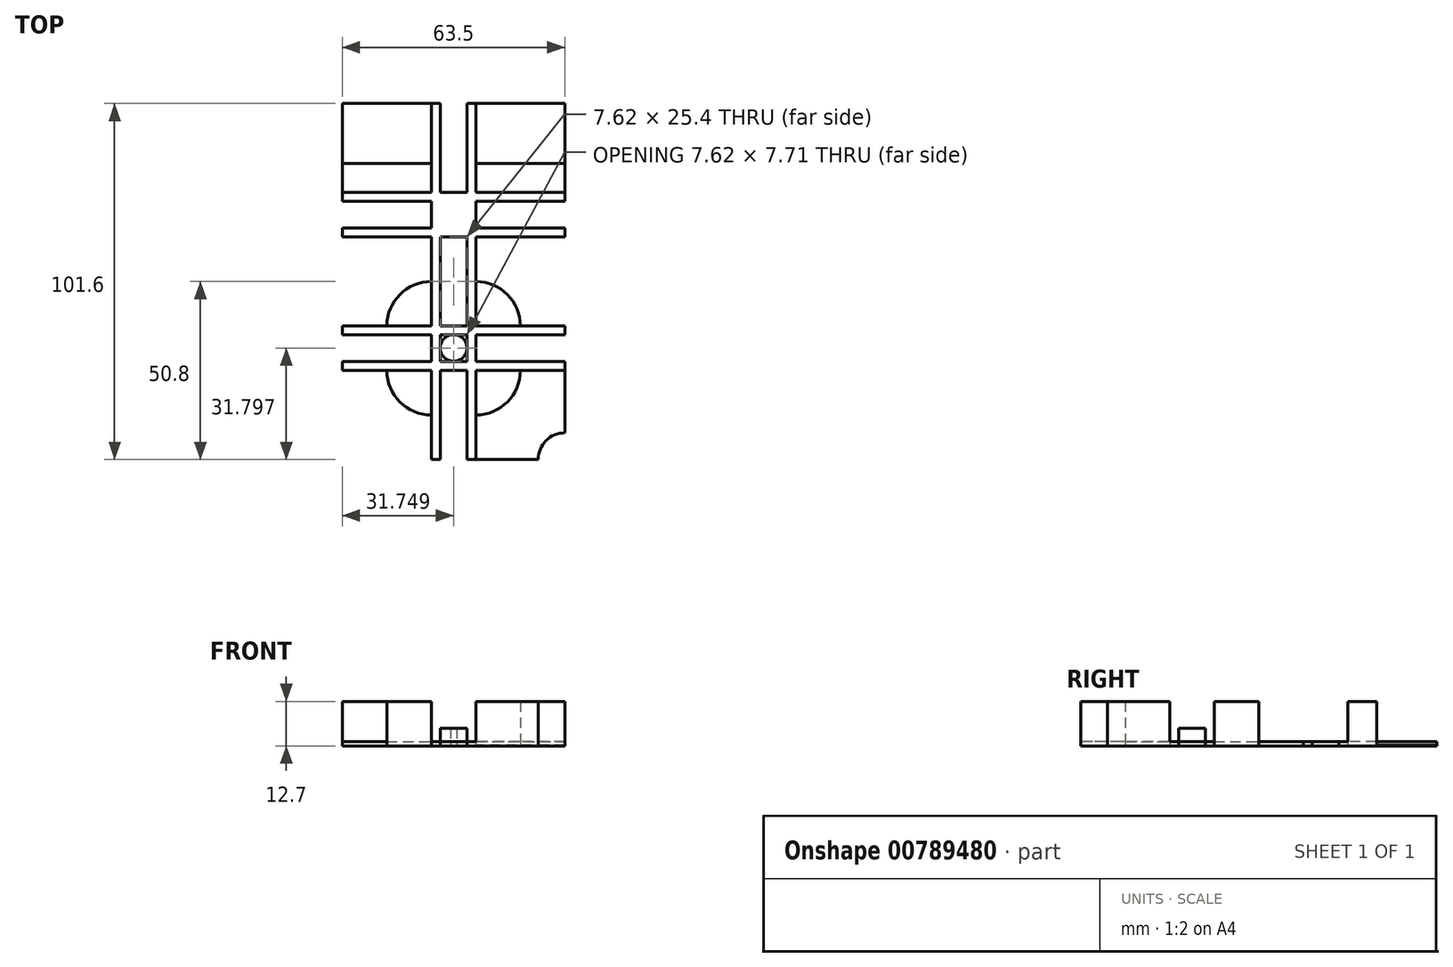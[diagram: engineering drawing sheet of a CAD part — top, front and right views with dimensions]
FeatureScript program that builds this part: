
annotation { "Feature Type Name" : "Feature", "Feature Type Description" : "" }
export const myFeature = defineFeature(function(context is Context, id is Id, definition is map)
    precondition{}
    {
        {
            var Q0;
            Q0=qCreatedBy(makeId("Top.planeOp"),FACE);
            var sketch = newSketch(context, id + "F0", { "sketchPlane" : qUnion([Q0])});
            skLineSegment(sketch, "E0.bottom", {"start": v(6.32, 50.8) * mm, "end": v(-19.08, 50.8) * mm});
            skLineSegment(sketch, "E0.top", {"start": v(6.32, 25.4) * mm, "end": v(-19.08, 25.4) * mm});
            skLineSegment(sketch, "E0.left", {"start": v(6.32, 50.8) * mm, "end": v(6.32, 25.4) * mm});
            skLineSegment(sketch, "E0.right", {"start": v(-19.08, 50.8) * mm, "end": v(-19.08, 25.4) * mm});
            skPoint(sketch, "E0.middle", {"position": v(-6.38, 38.1) * mm});
            skLineSegment(sketch, "E1.bottom", {"start": v(44.42, 25.4) * mm, "end": v(19.02, 25.4) * mm});
            skLineSegment(sketch, "E1.top", {"start": v(44.42, 50.8) * mm, "end": v(19.02, 50.8) * mm});
            skLineSegment(sketch, "E1.left", {"start": v(44.42, 25.4) * mm, "end": v(44.42, 50.8) * mm});
            skLineSegment(sketch, "E1.right", {"start": v(19.02, 25.4) * mm, "end": v(19.02, 50.8) * mm});
            skPoint(sketch, "E1.middle", {"position": v(31.72, 38.1) * mm});
            skLineSegment(sketch, "E2.bottom", {"start": v(-19.08, -12.7) * mm, "end": v(6.32, -12.7) * mm});
            skLineSegment(sketch, "E2.top", {"start": v(-19.08, 12.7) * mm, "end": v(6.32, 12.7) * mm});
            skLineSegment(sketch, "E2.left", {"start": v(-19.08, -12.7) * mm, "end": v(-19.08, 12.7) * mm});
            skLineSegment(sketch, "E2.right", {"start": v(6.32, -12.7) * mm, "end": v(6.32, 12.7) * mm});
            skPoint(sketch, "E2.middle", {"position": v(-6.38, 0) * mm});
            skLineSegment(sketch, "E3.bottom", {"start": v(44.42, -12.7) * mm, "end": v(19.02, -12.7) * mm});
            skLineSegment(sketch, "E3.top", {"start": v(44.42, 12.7) * mm, "end": v(19.02, 12.7) * mm});
            skLineSegment(sketch, "E3.left", {"start": v(44.42, -12.7) * mm, "end": v(44.42, 12.7) * mm});
            skLineSegment(sketch, "E3.right", {"start": v(19.02, -12.7) * mm, "end": v(19.02, 12.7) * mm});
            skPoint(sketch, "E3.middle", {"position": v(31.72, 0) * mm});
            skLineSegment(sketch, "E4.bottom", {"start": v(44.42, -50.8) * mm, "end": v(19.02, -50.8) * mm});
            skLineSegment(sketch, "E4.top", {"start": v(44.42, -25.4) * mm, "end": v(19.02, -25.4) * mm});
            skLineSegment(sketch, "E4.left", {"start": v(44.42, -50.8) * mm, "end": v(44.42, -25.4) * mm});
            skLineSegment(sketch, "E4.right", {"start": v(19.02, -50.8) * mm, "end": v(19.02, -25.4) * mm});
            skPoint(sketch, "E4.middle", {"position": v(31.72, -38.1) * mm});
            skPoint(sketch, "E4.middle.positionSnap0", {"position": v(31.72, -12.7) * mm});
            skPoint(sketch, "E4.centerSnap0", {"position": v(31.72, -12.7) * mm});
            skLineSegment(sketch, "E5.bottom", {"start": v(-19.08, -25.4) * mm, "end": v(6.32, -25.4) * mm});
            skLineSegment(sketch, "E5.top", {"start": v(-19.08, -50.8) * mm, "end": v(6.32, -50.8) * mm});
            skLineSegment(sketch, "E5.left", {"start": v(-19.08, -25.4) * mm, "end": v(-19.08, -50.8) * mm});
            skLineSegment(sketch, "E5.right", {"start": v(6.32, -25.4) * mm, "end": v(6.32, -50.8) * mm});
            skPoint(sketch, "E5.middle", {"position": v(-6.38, -38.1) * mm});
            skPoint(sketch, "E5.middle.positionSnap0", {"position": v(-6.38, -12.7) * mm});
            skPoint(sketch, "E5.middle.positionSnap1", {"position": v(19.02, -38.1) * mm});
            skPoint(sketch, "E5.centerSnap0", {"position": v(-6.38, -12.7) * mm});
            skPoint(sketch, "E5.centerSnap1", {"position": v(19.02, -38.1) * mm});
            skLineSegment(sketch, "E6.bottom", {"start": v(6.32, 50.8) * mm, "end": v(8.86, 50.8) * mm});
            skLineSegment(sketch, "E6.top", {"start": v(6.32, -50.8) * mm, "end": v(8.86, -50.8) * mm});
            skLineSegment(sketch, "E6.left", {"start": v(6.32, 50.8) * mm, "end": v(6.32, -50.8) * mm});
            skLineSegment(sketch, "E6.right", {"start": v(8.86, 50.8) * mm, "end": v(8.86, -50.8) * mm});
            skLineSegment(sketch, "E7.bottom", {"start": v(19.02, 50.8) * mm, "end": v(16.48, 50.8) * mm});
            skLineSegment(sketch, "E7.top", {"start": v(19.02, -50.8) * mm, "end": v(16.48, -50.8) * mm});
            skLineSegment(sketch, "E7.left", {"start": v(19.02, 50.8) * mm, "end": v(19.02, -50.8) * mm});
            skLineSegment(sketch, "E7.right", {"start": v(16.48, 50.8) * mm, "end": v(16.48, -50.8) * mm});
            skLineSegment(sketch, "E8.bottom", {"start": v(-19.08, 25.4) * mm, "end": v(44.42, 25.4) * mm});
            skLineSegment(sketch, "E8.top", {"start": v(-19.08, 22.86) * mm, "end": v(44.42, 22.86) * mm});
            skLineSegment(sketch, "E8.left", {"start": v(-19.08, 25.4) * mm, "end": v(-19.08, 22.86) * mm});
            skLineSegment(sketch, "E8.right", {"start": v(44.42, 25.4) * mm, "end": v(44.42, 22.86) * mm});
            skLineSegment(sketch, "E9.bottom", {"start": v(-19.08, 12.7) * mm, "end": v(44.42, 12.7) * mm});
            skLineSegment(sketch, "E9.top", {"start": v(-19.08, 15.24) * mm, "end": v(44.42, 15.24) * mm});
            skLineSegment(sketch, "E9.left", {"start": v(-19.08, 12.7) * mm, "end": v(-19.08, 15.24) * mm});
            skLineSegment(sketch, "E9.right", {"start": v(44.42, 12.7) * mm, "end": v(44.42, 15.24) * mm});
            skLineSegment(sketch, "E10.bottom", {"start": v(-19.08, -25.4) * mm, "end": v(44.42, -25.4) * mm});
            skLineSegment(sketch, "E10.top", {"start": v(-19.08, -22.86) * mm, "end": v(44.42, -22.86) * mm});
            skLineSegment(sketch, "E10.left", {"start": v(-19.08, -25.4) * mm, "end": v(-19.08, -22.86) * mm});
            skLineSegment(sketch, "E10.right", {"start": v(44.42, -25.4) * mm, "end": v(44.42, -22.86) * mm});
            skLineSegment(sketch, "E11.bottom", {"start": v(-19.08, -12.7) * mm, "end": v(44.42, -12.7) * mm});
            skLineSegment(sketch, "E11.top", {"start": v(-19.08, -15.24) * mm, "end": v(44.42, -15.24) * mm});
            skLineSegment(sketch, "E11.left", {"start": v(-19.08, -12.7) * mm, "end": v(-19.08, -15.24) * mm});
            skLineSegment(sketch, "E11.right", {"start": v(44.42, -12.7) * mm, "end": v(44.42, -15.24) * mm});
            skCircle(sketch, "E12", {"center": v(12.67, -18.95) * mm, "radius": 3.81 * mm});
            skPoint(sketch, "E12.centerSnap0", {"position": v(12.67, -15.24) * mm});
            skLineSegment(sketch, "E13", {"start": v(-19.08, 33.65) * mm, "end": v(6.32, 33.65) * mm});
            skLineSegment(sketch, "E14", {"start": v(19.02, 33.65) * mm, "end": v(44.42, 33.65) * mm});
            skArc(sketch, "E15", {"start": v(-2.7, -3.75) * mm, "mid": v(1.44, -0.98) * mm, "end": v(6.32, 0) * mm});
            skArc(sketch, "E16", {"start": v(-2.7, -3.75) * mm, "mid": v(-5.42, -7.86) * mm, "end": v(-6.38, -12.7) * mm});
            skArc(sketch, "E17", {"start": v(28.34, -4.08) * mm, "mid": v(30.85, -8.07) * mm, "end": v(31.72, -12.7) * mm});
            skArc(sketch, "E18", {"start": v(28.34, -4.08) * mm, "mid": v(24.1, -1.06) * mm, "end": v(19.02, 0) * mm});
            skArc(sketch, "E19", {"start": v(-1.73, -35.23) * mm, "mid": v(-5.16, -30.84) * mm, "end": v(-6.38, -25.4) * mm});
            skArc(sketch, "E20", {"start": v(-1.73, -35.23) * mm, "mid": v(2.05, -37.36) * mm, "end": v(6.32, -38.1) * mm});
            skArc(sketch, "E21", {"start": v(28.65, -33.67) * mm, "mid": v(30.93, -29.81) * mm, "end": v(31.72, -25.4) * mm});
            skArc(sketch, "E22", {"start": v(28.65, -33.67) * mm, "mid": v(24.32, -36.94) * mm, "end": v(19.02, -38.1) * mm});
            skArc(sketch, "E23", {"start": v(39.2, -45.25) * mm, "mid": v(41.6, -43.72) * mm, "end": v(44.42, -43.18) * mm});
            skArc(sketch, "E24", {"start": v(39.2, -45.25) * mm, "mid": v(37.42, -47.78) * mm, "end": v(36.8, -50.8) * mm});
            skArc(sketch, "E25", {"start": v(-13.68, -45.43) * mm, "mid": v(-12.04, -47.9) * mm, "end": v(-11.46, -50.8) * mm});
            skArc(sketch, "E26", {"start": v(-13.68, -45.43) * mm, "mid": v(-16.16, -43.76) * mm, "end": v(-19.08, -43.18) * mm});
            skArc(sketch, "E27", {"start": v(38.84, 7.5) * mm, "mid": v(37.33, 9.9) * mm, "end": v(36.8, 12.7) * mm});
            skArc(sketch, "E28", {"start": v(38.84, 7.5) * mm, "mid": v(41.38, 5.71) * mm, "end": v(44.42, 5.08) * mm});
            skArc(sketch, "E29", {"start": v(-13.86, 7.15) * mm, "mid": v(-12.09, 9.68) * mm, "end": v(-11.46, 12.7) * mm});
            skArc(sketch, "E30", {"start": v(-13.86, 7.15) * mm, "mid": v(-16.27, 5.62) * mm, "end": v(-19.08, 5.08) * mm});
            skSolve(sketch);
        }
        {
            var Q0;
            {var subQ0=sQuery(id+"F0.wireOp",EDGE,"E12");var subQ1=sQuery(id+"F0.wireOp",EDGE,"E11.top");var subQ2=makeQuery(id+"F0.imprint","INTERSECT",VERTEX,{"disambiguationData":[OD(0.0)],"derivedFrom":[subQ1,subQ0]});Q0=makeQuery(id+"F0.imprint","IMPRINT",FACE,{"disambiguationData":[TD([[makeQuery(id+"F0.imprint","IMPRINT",EDGE,{"disambiguationData":[TD([[subQ2,1.0]])],"derivedFrom":subQ1}),-1.0]])]});}
            extrude(context, id + "F1", {"entities" : qUnion([Q0]), "depth" : 5.08 * mm, "offsetDistance" : 25.4 * mm});
        }
        {
            var Q0;
            {var subQ0=sQuery(id+"F0.wireOp",EDGE,"E6.bottom");Q0=makeQuery(id+"F0.imprint","IMPRINT",FACE,{"disambiguationData":[TD([[makeQuery(id+"F0.imprint","IMPRINT",EDGE,{"derivedFrom":subQ0}),-1.0]])]});}
            var Q1;
            {var subQ0=sQuery(id+"F0.wireOp",EDGE,"E7.bottom");Q1=makeQuery(id+"F0.imprint","IMPRINT",FACE,{"disambiguationData":[TD([[makeQuery(id+"F0.imprint","IMPRINT",EDGE,{"derivedFrom":subQ0}),1.0]])]});}
            var Q2;
            {var subQ0=sQuery(id+"F0.wireOp",EDGE,"E8.top");var subQ1=sQuery(id+"F0.wireOp",EDGE,"E6.right");var subQ2=makeQuery(id+"F0.imprint","INTERSECT",VERTEX,{"derivedFrom":[subQ1,subQ0]});Q2=makeQuery(id+"F0.imprint","IMPRINT",FACE,{"disambiguationData":[TD([[makeQuery(id+"F0.imprint","IMPRINT",EDGE,{"disambiguationData":[TD([[subQ2,-1.0]])],"derivedFrom":subQ1}),1.0]])]});}
            var Q3;
            {var subQ0=sQuery(id+"F0.wireOp",EDGE,"E8.bottom");var subQ1=sQuery(id+"F0.wireOp",EDGE,"E6.right");var subQ2=makeQuery(id+"F0.imprint","INTERSECT",VERTEX,{"derivedFrom":[subQ1,subQ0]});Q3=makeQuery(id+"F0.imprint","IMPRINT",FACE,{"disambiguationData":[TD([[makeQuery(id+"F0.imprint","IMPRINT",EDGE,{"disambiguationData":[TD([[subQ2,-1.0]])],"derivedFrom":subQ1}),1.0]])]});}
            var Q4;
            {var subQ0=sQuery(id+"F0.wireOp",EDGE,"E8.bottom");var subQ5=sQuery(id+"F0.wireOp",EDGE,"E6.right");var subQ6=makeQuery(id+"F0.imprint","INTERSECT",VERTEX,{"derivedFrom":[subQ5,subQ0]});Q4=makeQuery(id+"F0.imprint","IMPRINT",FACE,{"disambiguationData":[TD([[makeQuery(id+"F0.imprint","IMPRINT",EDGE,{"disambiguationData":[TD([[subQ6,-1.0]])],"derivedFrom":subQ5}),-1.0]])]});}
            var Q5;
            {var subQ0=sQuery(id+"F0.wireOp",EDGE,"E0.top");Q5=makeQuery(id+"F0.imprint","IMPRINT",FACE,{"disambiguationData":[TD([[makeQuery(id+"F0.imprint","IMPRINT",EDGE,{"derivedFrom":subQ0}),1.0]])]});}
            var Q6;
            {var subQ0=sQuery(id+"F0.wireOp",EDGE,"E9.top");var subQ1=sQuery(id+"F0.wireOp",EDGE,"E6.left");var subQ2=makeQuery(id+"F0.imprint","INTERSECT",VERTEX,{"derivedFrom":[subQ1,subQ0]});Q6=makeQuery(id+"F0.imprint","IMPRINT",FACE,{"disambiguationData":[TD([[makeQuery(id+"F0.imprint","IMPRINT",EDGE,{"disambiguationData":[TD([[subQ2,1.0]])],"derivedFrom":subQ1}),1.0]])]});}
            var Q7;
            {var subQ0=sQuery(id+"F0.wireOp",EDGE,"E8.top");var subQ1=sQuery(id+"F0.wireOp",EDGE,"E7.left");var subQ2=makeQuery(id+"F0.imprint","INTERSECT",VERTEX,{"derivedFrom":[subQ1,subQ0]});Q7=makeQuery(id+"F0.imprint","IMPRINT",FACE,{"disambiguationData":[TD([[makeQuery(id+"F0.imprint","IMPRINT",EDGE,{"disambiguationData":[TD([[subQ2,-1.0]])],"derivedFrom":subQ1}),-1.0]])]});}
            var Q8;
            {var subQ0=sQuery(id+"F0.wireOp",EDGE,"E1.bottom");Q8=makeQuery(id+"F0.imprint","IMPRINT",FACE,{"disambiguationData":[TD([[makeQuery(id+"F0.imprint","IMPRINT",EDGE,{"derivedFrom":subQ0}),1.0]])]});}
            var Q9;
            {var subQ0=sQuery(id+"F0.wireOp",EDGE,"E8.bottom");var subQ5=sQuery(id+"F0.wireOp",EDGE,"E7.right");var subQ6=makeQuery(id+"F0.imprint","INTERSECT",VERTEX,{"derivedFrom":[subQ5,subQ0]});Q9=makeQuery(id+"F0.imprint","IMPRINT",FACE,{"disambiguationData":[TD([[makeQuery(id+"F0.imprint","IMPRINT",EDGE,{"disambiguationData":[TD([[subQ6,-1.0]])],"derivedFrom":subQ5}),1.0]])]});}
            var Q10;
            {var subQ0=sQuery(id+"F0.wireOp",EDGE,"E9.right");Q10=makeQuery(id+"F0.imprint","IMPRINT",FACE,{"disambiguationData":[TD([[makeQuery(id+"F0.imprint","IMPRINT",EDGE,{"derivedFrom":subQ0}),1.0]])]});}
            var Q11;
            {var subQ0=sQuery(id+"F0.wireOp",EDGE,"E9.bottom");var subQ5=sQuery(id+"F0.wireOp",EDGE,"E7.right");var subQ6=makeQuery(id+"F0.imprint","INTERSECT",VERTEX,{"derivedFrom":[subQ5,subQ0]});Q11=makeQuery(id+"F0.imprint","IMPRINT",FACE,{"disambiguationData":[TD([[makeQuery(id+"F0.imprint","IMPRINT",EDGE,{"disambiguationData":[TD([[subQ6,1.0]])],"derivedFrom":subQ5}),1.0]])]});}
            var Q12;
            {var subQ3=sQuery(id+"F0.wireOp",EDGE,"E9.bottom");var subQ5=sQuery(id+"F0.wireOp",EDGE,"E6.right");var subQ6=makeQuery(id+"F0.imprint","INTERSECT",VERTEX,{"derivedFrom":[subQ5,subQ3]});Q12=makeQuery(id+"F0.imprint","IMPRINT",FACE,{"disambiguationData":[TD([[makeQuery(id+"F0.imprint","IMPRINT",EDGE,{"disambiguationData":[TD([[subQ6,1.0]])],"derivedFrom":subQ5}),-1.0]])]});}
            var Q13;
            {var subQ0=sQuery(id+"F0.wireOp",EDGE,"E9.left");Q13=makeQuery(id+"F0.imprint","IMPRINT",FACE,{"disambiguationData":[TD([[makeQuery(id+"F0.imprint","IMPRINT",EDGE,{"derivedFrom":subQ0}),-1.0]])]});}
            var Q14;
            {var subQ0=sQuery(id+"F0.wireOp",EDGE,"E9.bottom");var subQ1=sQuery(id+"F0.wireOp",EDGE,"E6.right");var subQ2=makeQuery(id+"F0.imprint","INTERSECT",VERTEX,{"derivedFrom":[subQ1,subQ0]});Q14=makeQuery(id+"F0.imprint","IMPRINT",FACE,{"disambiguationData":[TD([[makeQuery(id+"F0.imprint","IMPRINT",EDGE,{"disambiguationData":[TD([[subQ2,1.0]])],"derivedFrom":subQ1}),1.0]])]});}
            var Q15;
            {var subQ0=sQuery(id+"F0.wireOp",EDGE,"E9.bottom");var subQ1=sQuery(id+"F0.wireOp",EDGE,"E6.right");var subQ2=makeQuery(id+"F0.imprint","INTERSECT",VERTEX,{"derivedFrom":[subQ1,subQ0]});Q15=makeQuery(id+"F0.imprint","IMPRINT",FACE,{"disambiguationData":[TD([[makeQuery(id+"F0.imprint","IMPRINT",EDGE,{"disambiguationData":[TD([[subQ2,-1.0]])],"derivedFrom":subQ1}),-1.0]])]});}
            var Q16;
            {var subQ0=sQuery(id+"F0.wireOp",EDGE,"E9.bottom");var subQ1=sQuery(id+"F0.wireOp",EDGE,"E7.right");var subQ2=makeQuery(id+"F0.imprint","INTERSECT",VERTEX,{"derivedFrom":[subQ1,subQ0]});Q16=makeQuery(id+"F0.imprint","IMPRINT",FACE,{"disambiguationData":[TD([[makeQuery(id+"F0.imprint","IMPRINT",EDGE,{"disambiguationData":[TD([[subQ2,-1.0]])],"derivedFrom":subQ1}),1.0]])]});}
            var Q17;
            {var subQ3=sQuery(id+"F0.wireOp",EDGE,"E11.left");Q17=makeQuery(id+"F0.imprint","IMPRINT",FACE,{"disambiguationData":[TD([[makeQuery(id+"F0.imprint","IMPRINT",EDGE,{"derivedFrom":subQ3}),1.0]])]});}
            var Q18;
            {var subQ0=sQuery(id+"F0.wireOp",EDGE,"E11.bottom");var subQ5=sQuery(id+"F0.wireOp",EDGE,"E6.right");var subQ6=makeQuery(id+"F0.imprint","INTERSECT",VERTEX,{"derivedFrom":[subQ5,subQ0]});Q18=makeQuery(id+"F0.imprint","IMPRINT",FACE,{"disambiguationData":[TD([[makeQuery(id+"F0.imprint","IMPRINT",EDGE,{"disambiguationData":[TD([[subQ6,-1.0]])],"derivedFrom":subQ5}),-1.0]])]});}
            var Q19;
            {var subQ0=sQuery(id+"F0.wireOp",EDGE,"E11.bottom");var subQ7=sQuery(id+"F0.wireOp",EDGE,"E6.right");var subQ8=makeQuery(id+"F0.imprint","INTERSECT",VERTEX,{"derivedFrom":[subQ7,subQ0]});Q19=makeQuery(id+"F0.imprint","IMPRINT",FACE,{"disambiguationData":[TD([[makeQuery(id+"F0.imprint","IMPRINT",EDGE,{"disambiguationData":[TD([[subQ8,-1.0]])],"derivedFrom":subQ7}),1.0]])]});}
            var Q20;
            {var subQ0=sQuery(id+"F0.wireOp",EDGE,"E11.bottom");var subQ5=sQuery(id+"F0.wireOp",EDGE,"E7.right");var subQ6=makeQuery(id+"F0.imprint","INTERSECT",VERTEX,{"derivedFrom":[subQ5,subQ0]});Q20=makeQuery(id+"F0.imprint","IMPRINT",FACE,{"disambiguationData":[TD([[makeQuery(id+"F0.imprint","IMPRINT",EDGE,{"disambiguationData":[TD([[subQ6,-1.0]])],"derivedFrom":subQ5}),1.0]])]});}
            var Q21;
            {var subQ3=sQuery(id+"F0.wireOp",EDGE,"E11.right");Q21=makeQuery(id+"F0.imprint","IMPRINT",FACE,{"disambiguationData":[TD([[makeQuery(id+"F0.imprint","IMPRINT",EDGE,{"derivedFrom":subQ3}),-1.0]])]});}
            var Q22;
            {var subQ1=sQuery(id+"F0.wireOp",EDGE,"E7.left");var subQ6=sQuery(id+"F0.wireOp",EDGE,"E11.top");var subQ7=makeQuery(id+"F0.imprint","INTERSECT",VERTEX,{"derivedFrom":[subQ1,subQ6]});Q22=makeQuery(id+"F0.imprint","IMPRINT",FACE,{"disambiguationData":[TD([[makeQuery(id+"F0.imprint","IMPRINT",EDGE,{"disambiguationData":[TD([[subQ7,-1.0]])],"derivedFrom":subQ1}),-1.0]])]});}
            var Q23;
            {var subQ2=sQuery(id+"F0.wireOp",EDGE,"E11.top");var subQ4=sQuery(id+"F0.wireOp",EDGE,"E6.left");var subQ5=makeQuery(id+"F0.imprint","INTERSECT",VERTEX,{"derivedFrom":[subQ4,subQ2]});Q23=makeQuery(id+"F0.imprint","IMPRINT",FACE,{"disambiguationData":[TD([[makeQuery(id+"F0.imprint","IMPRINT",EDGE,{"disambiguationData":[TD([[subQ5,-1.0]])],"derivedFrom":subQ4}),1.0]])]});}
            var Q24;
            {var subQ0=sQuery(id+"F0.wireOp",EDGE,"E10.bottom");var subQ1=sQuery(id+"F0.wireOp",EDGE,"E6.right");var subQ2=makeQuery(id+"F0.imprint","INTERSECT",VERTEX,{"derivedFrom":[subQ1,subQ0]});Q24=makeQuery(id+"F0.imprint","IMPRINT",FACE,{"disambiguationData":[TD([[makeQuery(id+"F0.imprint","IMPRINT",EDGE,{"disambiguationData":[TD([[subQ2,1.0]])],"derivedFrom":subQ1}),1.0]])]});}
            var Q25;
            {var subQ0=sQuery(id+"F0.wireOp",EDGE,"E10.bottom");var subQ5=sQuery(id+"F0.wireOp",EDGE,"E6.right");var subQ6=makeQuery(id+"F0.imprint","INTERSECT",VERTEX,{"derivedFrom":[subQ5,subQ0]});Q25=makeQuery(id+"F0.imprint","IMPRINT",FACE,{"disambiguationData":[TD([[makeQuery(id+"F0.imprint","IMPRINT",EDGE,{"disambiguationData":[TD([[subQ6,1.0]])],"derivedFrom":subQ5}),-1.0]])]});}
            var Q26;
            {var subQ0=sQuery(id+"F0.wireOp",EDGE,"E10.left");Q26=makeQuery(id+"F0.imprint","IMPRINT",FACE,{"disambiguationData":[TD([[makeQuery(id+"F0.imprint","IMPRINT",EDGE,{"derivedFrom":subQ0}),-1.0]])]});}
            var Q27;
            {var subQ3=sQuery(id+"F0.wireOp",EDGE,"E10.right");Q27=makeQuery(id+"F0.imprint","IMPRINT",FACE,{"disambiguationData":[TD([[makeQuery(id+"F0.imprint","IMPRINT",EDGE,{"derivedFrom":subQ3}),1.0]])]});}
            var Q28;
            {var subQ0=sQuery(id+"F0.wireOp",EDGE,"E10.bottom");var subQ5=sQuery(id+"F0.wireOp",EDGE,"E7.right");var subQ6=makeQuery(id+"F0.imprint","INTERSECT",VERTEX,{"derivedFrom":[subQ5,subQ0]});Q28=makeQuery(id+"F0.imprint","IMPRINT",FACE,{"disambiguationData":[TD([[makeQuery(id+"F0.imprint","IMPRINT",EDGE,{"disambiguationData":[TD([[subQ6,1.0]])],"derivedFrom":subQ5}),1.0]])]});}
            var Q29;
            {var subQ1=sQuery(id+"F0.wireOp",EDGE,"E7.top");Q29=makeQuery(id+"F0.imprint","IMPRINT",FACE,{"disambiguationData":[TD([[makeQuery(id+"F0.imprint","IMPRINT",EDGE,{"derivedFrom":subQ1}),-1.0]])]});}
            var Q30;
            {var subQ0=sQuery(id+"F0.wireOp",EDGE,"E6.top");Q30=makeQuery(id+"F0.imprint","IMPRINT",FACE,{"disambiguationData":[TD([[makeQuery(id+"F0.imprint","IMPRINT",EDGE,{"derivedFrom":subQ0}),1.0]])]});}
            extrude(context, id + "F2", {"entities" : qUnion([Q0, Q1, Q2, Q3, Q4, Q5, Q6, Q7, Q8, Q9, Q10, Q11, Q12, Q13, Q14, Q15, Q16, Q17, Q18, Q19, Q20, Q21, Q22, Q23, Q24, Q25, Q26, Q27, Q28, Q29, Q30]), "depth" : 1.27 * mm, "offsetDistance" : 25.4 * mm});
        }
        {
            var Q0;
            {var subQ0=sQuery(id+"F0.wireOp",EDGE,"E0.top");Q0=makeQuery(id+"F0.imprint","IMPRINT",FACE,{"disambiguationData":[TD([[makeQuery(id+"F0.imprint","IMPRINT",EDGE,{"derivedFrom":subQ0}),-1.0]])]});}
            var Q1;
            {var subQ0=sQuery(id+"F0.wireOp",EDGE,"E1.bottom");Q1=makeQuery(id+"F0.imprint","IMPRINT",FACE,{"disambiguationData":[TD([[makeQuery(id+"F0.imprint","IMPRINT",EDGE,{"derivedFrom":subQ0}),-1.0]])]});}
            var Q2;
            {var subQ0=sQuery(id+"F0.wireOp",EDGE,"E15");Q2=makeQuery(id+"F0.imprint","IMPRINT",FACE,{"disambiguationData":[TD([[makeQuery(id+"F0.imprint","IMPRINT",EDGE,{"derivedFrom":subQ0}),1.0]])]});}
            var Q3;
            {var subQ9=sQuery(id+"F0.wireOp",EDGE,"E17");Q3=makeQuery(id+"F0.imprint","IMPRINT",FACE,{"disambiguationData":[TD([[makeQuery(id+"F0.imprint","IMPRINT",EDGE,{"derivedFrom":subQ9}),1.0]])]});}
            var Q4;
            {var subQ8=sQuery(id+"F0.wireOp",EDGE,"E21");Q4=makeQuery(id+"F0.imprint","IMPRINT",FACE,{"disambiguationData":[TD([[makeQuery(id+"F0.imprint","IMPRINT",EDGE,{"derivedFrom":subQ8}),-1.0]])]});}
            var Q5;
            {var subQ9=sQuery(id+"F0.wireOp",EDGE,"E19");Q5=makeQuery(id+"F0.imprint","IMPRINT",FACE,{"disambiguationData":[TD([[makeQuery(id+"F0.imprint","IMPRINT",EDGE,{"derivedFrom":subQ9}),1.0]])]});}
            extrude(context, id + "F3", {"entities" : qUnion([Q0, Q1, Q2, Q3, Q4, Q5]), "operationType" : NewBodyOperationType.ADD, "depth" : 12.7 * mm, "offsetDistance" : 25.4 * mm});
        }
        {
            var Q0;
            {var subQ0=sQuery(id+"F0.wireOp",EDGE,"E0.bottom");Q0=makeQuery(id+"F0.imprint","IMPRINT",FACE,{"disambiguationData":[TD([[makeQuery(id+"F0.imprint","IMPRINT",EDGE,{"derivedFrom":subQ0}),1.0]])]});}
            var Q1;
            {var subQ0=sQuery(id+"F0.wireOp",EDGE,"E1.top");Q1=makeQuery(id+"F0.imprint","IMPRINT",FACE,{"disambiguationData":[TD([[makeQuery(id+"F0.imprint","IMPRINT",EDGE,{"derivedFrom":subQ0}),1.0]])]});}
            extrude(context, id + "F4", {"entities" : qUnion([Q0, Q1]), "operationType" : NewBodyOperationType.ADD, "depth" : 0.25 * mm, "offsetDistance" : 25.4 * mm});
        }
    });
